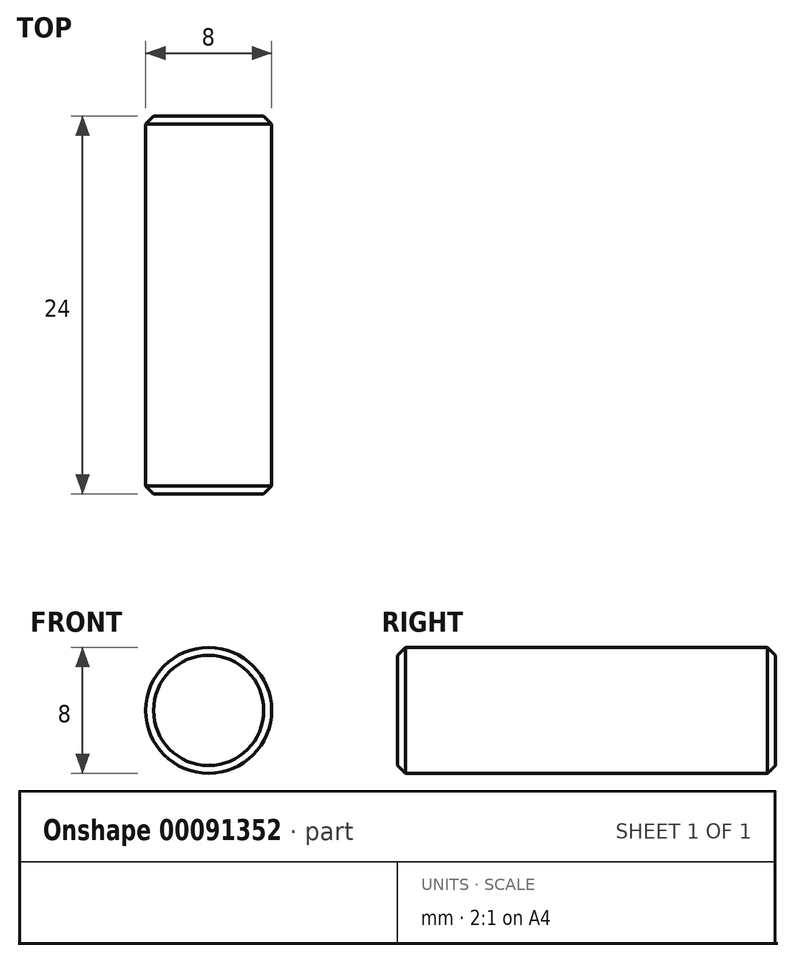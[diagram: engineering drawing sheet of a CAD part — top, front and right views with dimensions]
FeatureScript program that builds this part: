
annotation { "Feature Type Name" : "Feature", "Feature Type Description" : "" }
export const myFeature = defineFeature(function(context is Context, id is Id, definition is map)
    precondition{}
    {
        {
            var Q0;
            Q0=qCreatedBy(makeId("Front.planeOp"),FACE);
            var sketch = newSketch(context, id + "F0", { "sketchPlane" : qUnion([Q0])});
            skCircle(sketch, "E0", {"center": v(0, 0) * mm, "radius": 4 * mm});
            skSolve(sketch);
        }
        {
            var Q0;
            Q0=makeQuery(id+"F0.imprint","IMPRINT",FACE,{"disambiguationData":[TD([[makeQuery(id+"F0.imprint","IMPRINT",EDGE,{"derivedFrom":sQuery(id+"F0.wireOp",EDGE,"E0")}),1.0]])]});
            extrude(context, id + "F1", {"entities" : qUnion([Q0]), "oppositeDirection" : true, "depth" : 24 * mm});
        }
        {
            var Q0;
            Q0=makeQuery(id+"F1.opExtrude","CAP_EDGE",EDGE,{"disambiguationData":[OSD([sQuery(id+"F0.wireOp",EDGE,"E0")])],"isStart":true});
            var Q1;
            Q1=makeQuery(id+"F1.opExtrude","CAP_EDGE",EDGE,{"disambiguationData":[OSD([sQuery(id+"F0.wireOp",EDGE,"E0")])],"isStart":false});
            chamfer(context, id + "F2", {"entities" : qUnion([Q0, Q1]), "width" : .5 * mm, "tangentPropagation" : true});
        }
    });
